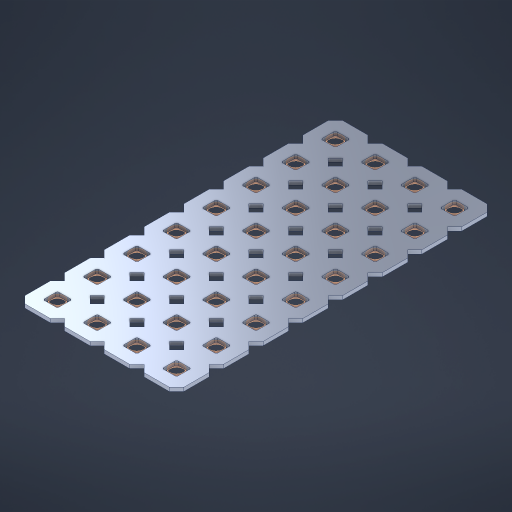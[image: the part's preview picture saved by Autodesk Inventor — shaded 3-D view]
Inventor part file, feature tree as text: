
AUTODESK INVENTOR PART (.ipt)
format: ipt  version: 2023 (Build 270158000, 158)  size: 633,344 bytes
history: native  units: in
note: dims shown in document units (in); Inventor stores cm internally (conversion verified against a paired STEP export)
features: other x33, extrude x31, sketch x2, pattern_linear x1
ambient origin geometry x8: Origin, YZ Plane, XZ Plane, XY Plane, X Axis, Y Axis, Z Axis, Center Point
bodies: Solid1 (feature_tree), Body (feature_tree)
feature tree (67):
  pattern_linear  "Rectangular Pattern1"  Spacing1=0.09in  [1 undecoded]
  sketch  "Sketch1"  dims[d1=0.5in]
  sketch  "Sketch2"  dims[d2=0.182in d3=0.09in d4=0.09in d5=0.09in d6=0.09in d7=0.09in d8=0.09in d9=0.09in d10=0.09in d11=0.02in d13=0.0in d14=0.172in d15=0.0625in d16=0.0in d19=0.5in d22=0.5in]
  other  "Srf1"
  other  "Srf126"
  other  "Srf127"
  other  "Srf128"
  other  "Srf129"
  other  "Srf130"
  other  "Srf131"
  other  "Srf250"
  other  "Srf268"
  other  "Srf269"
  other  "Srf270"
  other  "Srf271"
  other  "Srf272"
  other  "Srf273"
  other  "Srf274"
  other  "Srf275"
  other  "Srf293"
  other  "Srf294"
  other  "Srf295"
  other  "Srf296"
  other  "Srf297"
  other  "Srf298"
  other  "Srf299"
  other  "Srf300"
  other  "Srf318"
  other  "Srf319"
  other  "Srf320"
  other  "Srf321"
  other  "Srf322"
  other  "Srf323"
  other  "Srf324"
  other  "Srf325"
  other  "Circle"
  extrude  "ExtrusionSrf126"  Depth=0.09in
  extrude  "ExtrusionSrf127"  Depth=0.09in
  extrude  "ExtrusionSrf128"  Depth=0.09in
  extrude  "ExtrusionSrf129"  Depth=0.09in
  extrude  "ExtrusionSrf130"  Depth=0.09in
  extrude  "ExtrusionSrf131"  Depth=0.09in
  extrude  "ExtrusionSrf250"  Depth=0.09in
  extrude  "ExtrusionSrf268"  Depth=0.02in
  extrude  "ExtrusionSrf269"  TaperAngle=0.0deg  [1 undecoded]
  extrude  "ExtrusionSrf270"  Depth=0.5in
  extrude  "ExtrusionSrf271"  Depth=0.5in TaperAngle=0.0deg
  extrude  "ExtrusionSrf272"  Depth=0.5in
  extrude  "ExtrusionSrf273"  Depth=0.5in
  extrude  "ExtrusionSrf274"  [1 undecoded]
  extrude  "ExtrusionSrf275"  [1 undecoded]
  extrude  "ExtrusionSrf293"  [1 undecoded]
  extrude  "ExtrusionSrf294"  [1 undecoded]
  extrude  "ExtrusionSrf295"  [1 undecoded]
  extrude  "ExtrusionSrf296"  [1 undecoded]
  extrude  "ExtrusionSrf297"  [1 undecoded]
  extrude  "ExtrusionSrf298"  [1 undecoded]
  extrude  "ExtrusionSrf299"  [1 undecoded]
  extrude  "ExtrusionSrf300"  [1 undecoded]
  extrude  "ExtrusionSrf318"  [1 undecoded]
  extrude  "ExtrusionSrf319"  [1 undecoded]
  extrude  "ExtrusionSrf320"  [1 undecoded]
  extrude  "ExtrusionSrf321"  [1 undecoded]
  extrude  "ExtrusionSrf322"  [1 undecoded]
  extrude  "ExtrusionSrf323"  [1 undecoded]
  extrude  "ExtrusionSrf324"  [1 undecoded]
  extrude  "ExtrusionSrf325"  [1 undecoded]
note: 20 required parameter values undecoded (feature->parameter linkage not recoverable at this tier; creation-order binding heuristic only, values carry confidence <= 0.55)
